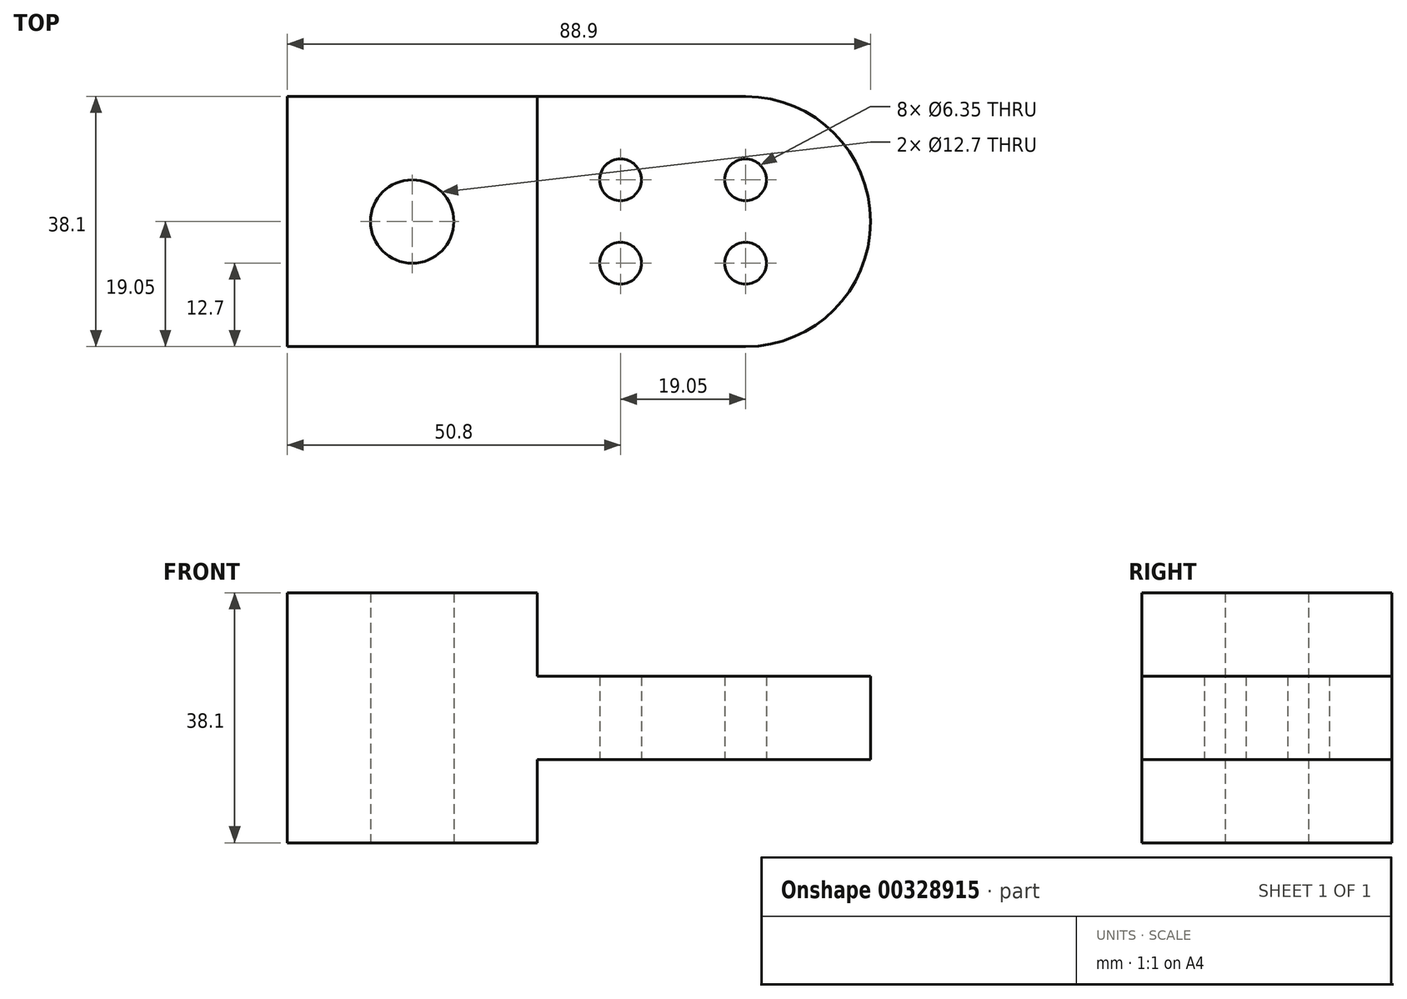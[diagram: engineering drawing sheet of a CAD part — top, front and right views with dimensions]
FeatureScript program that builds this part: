
annotation { "Feature Type Name" : "Feature", "Feature Type Description" : "" }
export const myFeature = defineFeature(function(context is Context, id is Id, definition is map)
    precondition{}
    {
        {
            var Q0;
            Q0=qCreatedBy(makeId("Top.planeOp"),FACE);
            var sketch = newSketch(context, id + "F0", { "sketchPlane" : qUnion([Q0])});
            skLineSegment(sketch, "E0.bottom", {"start": v(0, 0) * mm, "end": v(38.1, 0) * mm});
            skLineSegment(sketch, "E0.top", {"start": v(0, 38.1) * mm, "end": v(38.1, 38.1) * mm});
            skLineSegment(sketch, "E0.left", {"start": v(0, 0) * mm, "end": v(0, 38.1) * mm});
            skLineSegment(sketch, "E0.right", {"start": v(38.1, 0) * mm, "end": v(38.1, 38.1) * mm});
            skLineSegment(sketch, "E1.bottom", {"start": v(38.1, 38.1) * mm, "end": v(69.85, 38.1) * mm});
            skLineSegment(sketch, "E1.top", {"start": v(38.1, 0) * mm, "end": v(69.85, 0) * mm});
            skLineSegment(sketch, "E1.left", {"start": v(38.1, 38.1) * mm, "end": v(38.1, 0) * mm});
            skArc(sketch, "E2", {"start": v(69.85, 0) * mm, "mid": v(88.9, 19.05) * mm, "end": v(69.85, 38.1) * mm});
            skCircle(sketch, "E3", {"center": v(19.05, 19.05) * mm, "radius": 6.35 * mm});
            skPoint(sketch, "E3.centerSnap0", {"position": v(0, 19.05) * mm});
            skPoint(sketch, "E3.centerSnap1", {"position": v(19.05, 38.1) * mm});
            skCircle(sketch, "E4", {"center": v(69.85, 25.4) * mm, "radius": 3.18 * mm});
            skCircle(sketch, "E5", {"center": v(69.85, 12.7) * mm, "radius": 3.18 * mm});
            skCircle(sketch, "E6", {"center": v(50.8, 25.4) * mm, "radius": 3.18 * mm});
            skCircle(sketch, "E7", {"center": v(50.8, 12.7) * mm, "radius": 3.18 * mm});
            skSolve(sketch);
        }
        {
            var Q0;
            Q0 = qSketchRegion(id + "F0", true);
            extrude(context, id + "F1", {"entities" : qUnion([Q0]), "depth" : 38.1 * mm});
        }
        {
            var Q0;
            Q0=makeQuery(id+"F0.imprint","IMPRINT",FACE,{"disambiguationData":[TD([[makeQuery(id+"F0.imprint","IMPRINT",EDGE,{"derivedFrom":sQuery(id+"F0.wireOp",EDGE,"E1.bottom")}),-1.0]])]});
            extrude(context, id + "F2", {"entities" : qUnion([Q0]), "operationType" : NewBodyOperationType.REMOVE, "depth" : 12.7 * mm});
        }
        {
            var Q0;
            Q0=makeQuery(id+"F1.opExtrude","CAP_FACE",FACE,{"disambiguationData":[OSD([sQuery(id+"F0.wireOp",EDGE,"E0.bottom"),sQuery(id+"F0.wireOp",EDGE,"E0.top"),sQuery(id+"F0.wireOp",EDGE,"E0.left"),sQuery(id+"F0.wireOp",EDGE,"E1.bottom"),sQuery(id+"F0.wireOp",EDGE,"E1.top"),sQuery(id+"F0.wireOp",EDGE,"E2"),sQuery(id+"F0.wireOp",EDGE,"E3"),sQuery(id+"F0.wireOp",EDGE,"E4"),sQuery(id+"F0.wireOp",EDGE,"E5"),sQuery(id+"F0.wireOp",EDGE,"E6"),sQuery(id+"F0.wireOp",EDGE,"E7")])],"isStart":false});
            var sketch = newSketch(context, id + "F3", { "sketchPlane" : qUnion([Q0])});
            skLineSegment(sketch, "E8", {"start": v(38.1, 38.1) * mm, "end": v(38.1, 0) * mm});
            skPoint(sketch, "E9", {"position": v(0, 38.1) * mm});
            skSolve(sketch);
        }
        {
            var Q0;
            {var subQ1=sQuery(id+"F3.wireOp",EDGE,"E8");Q0=makeQuery(id+"F3.imprint","IMPRINT",FACE,{"disambiguationData":[TD([[makeQuery(id+"F3.imprint","IMPRINT",EDGE,{"derivedFrom":subQ1}),1.0]])]});}
            extrude(context, id + "F4", {"entities" : qUnion([Q0]), "operationType" : NewBodyOperationType.REMOVE, "oppositeDirection" : true, "depth" : 12.7 * mm});
        }
        {
            var Q0;
            Q0=makeQuery(id+"F1.opExtrude","SWEPT_BODY",BODY,{"disambiguationData":[OSD([sQuery(id+"F0.wireOp",EDGE,"E0.bottom"),sQuery(id+"F0.wireOp",EDGE,"E0.top"),sQuery(id+"F0.wireOp",EDGE,"E0.left"),sQuery(id+"F0.wireOp",EDGE,"E1.bottom"),sQuery(id+"F0.wireOp",EDGE,"E1.top"),sQuery(id+"F0.wireOp",EDGE,"E2"),sQuery(id+"F0.wireOp",EDGE,"E3"),sQuery(id+"F0.wireOp",EDGE,"E4"),sQuery(id+"F0.wireOp",EDGE,"E5"),sQuery(id+"F0.wireOp",EDGE,"E6"),sQuery(id+"F0.wireOp",EDGE,"E7")])]});
            transform(context, id + "F5", {"entities" : qUnion([Q0]), "transformType" : TransformType.TRANSLATION_3D, "dx" : 0 * mm, "dy" : 0 * mm, "dz" : 0 * mm, "makeCopy" : true});
        }
    });
